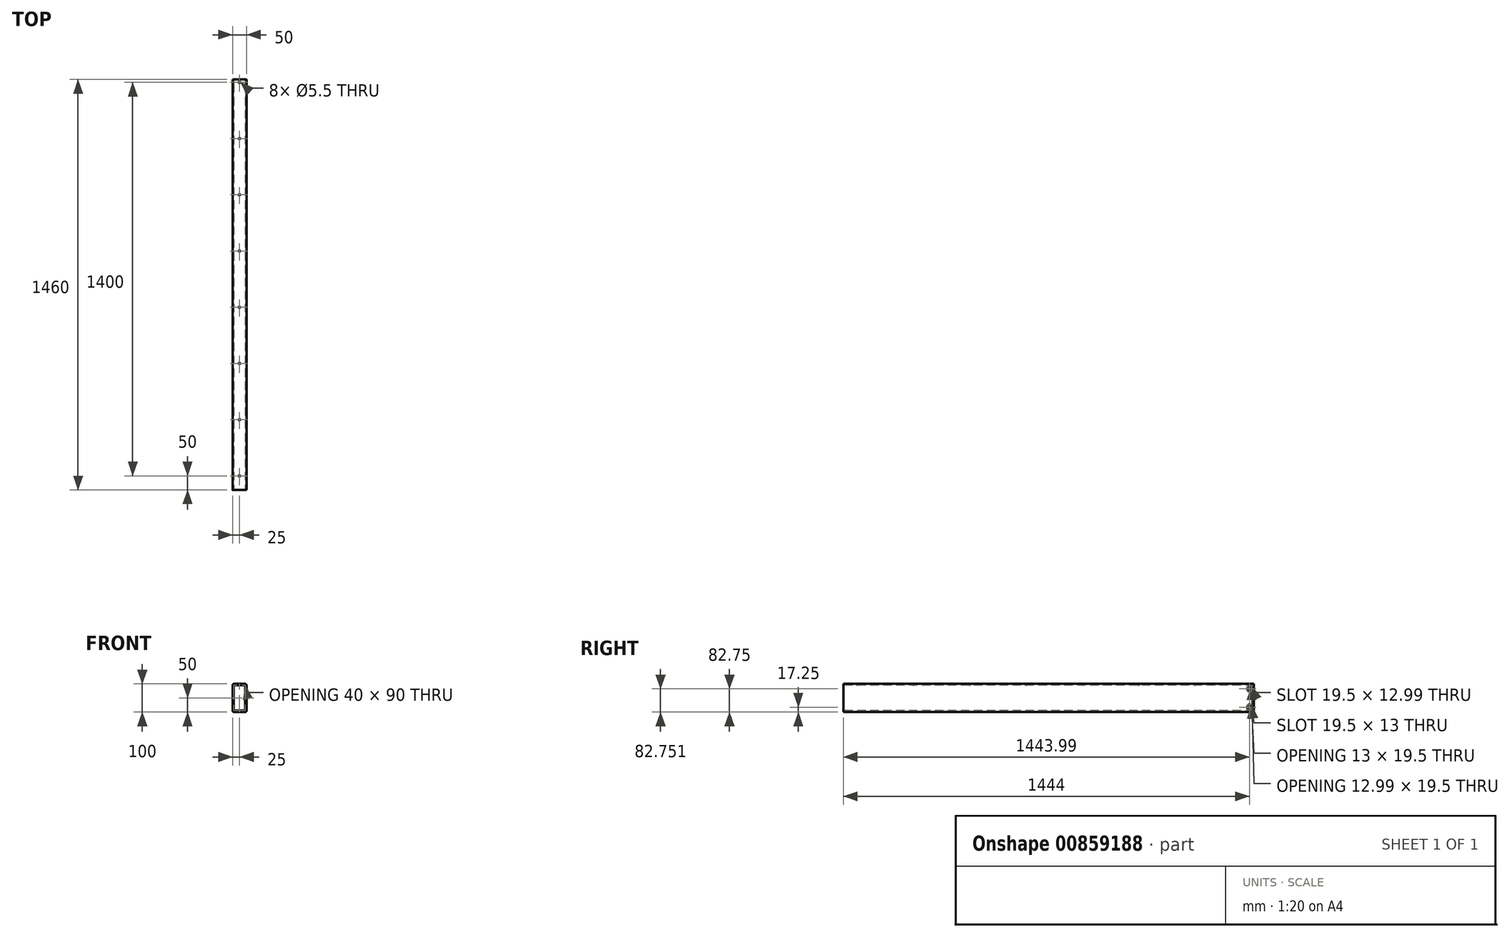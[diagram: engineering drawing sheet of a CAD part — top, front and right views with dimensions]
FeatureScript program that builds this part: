
annotation { "Feature Type Name" : "Feature", "Feature Type Description" : "" }
export const myFeature = defineFeature(function(context is Context, id is Id, definition is map)
    precondition{}
    {
        {
            var Q0;
            Q0=qCreatedBy(makeId("Front.planeOp"),FACE);
            var sketch = newSketch(context, id + "F0", { "sketchPlane" : qUnion([Q0])});
            skLineSegment(sketch, "E0.bottom", {"start": v(20, -50) * mm, "end": v(-20, -50) * mm});
            skLineSegment(sketch, "E0.top", {"start": v(20, 50) * mm, "end": v(-20, 50) * mm});
            skLineSegment(sketch, "E0.left", {"start": v(25, -45) * mm, "end": v(25, 45) * mm});
            skLineSegment(sketch, "E0.right", {"start": v(-25, -45) * mm, "end": v(-25, 45) * mm});
            skPoint(sketch, "E0.middle", {"position": v(0, 0) * mm});
            skPoint(sketch, "E1.visualSharp", {"position": v(-25, 50) * mm});
            skArc(sketch, "E1.filletArc", {"start": v(-20, 50) * mm, "mid": v(-23.54, 48.54) * mm, "end": v(-25, 45) * mm});
            skPoint(sketch, "E2.visualSharp", {"position": v(25, 50) * mm});
            skArc(sketch, "E2.filletArc", {"start": v(25, 45) * mm, "mid": v(23.54, 48.54) * mm, "end": v(20, 50) * mm});
            skPoint(sketch, "E3.visualSharp", {"position": v(-25, -50) * mm});
            skArc(sketch, "E3.filletArc", {"start": v(-25, -45) * mm, "mid": v(-23.54, -48.54) * mm, "end": v(-20, -50) * mm});
            skPoint(sketch, "E4.visualSharp", {"position": v(25, -50) * mm});
            skArc(sketch, "E4.filletArc", {"start": v(20, -50) * mm, "mid": v(23.54, -48.54) * mm, "end": v(25, -45) * mm});
            skLineSegment(sketch, "E5.0", {"start": v(-20, -42.5) * mm, "end": v(-20, 42.5) * mm});
            skLineSegment(sketch, "E5.1", {"start": v(17.5, -45) * mm, "end": v(-17.5, -45) * mm});
            skLineSegment(sketch, "E5.2", {"start": v(20, -42.5) * mm, "end": v(20, 42.5) * mm});
            skLineSegment(sketch, "E5.3", {"start": v(17.5, 45) * mm, "end": v(-17.5, 45) * mm});
            skArc(sketch, "E6.filletArc", {"start": v(-17.5, 45) * mm, "mid": v(-19.27, 44.27) * mm, "end": v(-20, 42.5) * mm});
            skArc(sketch, "E7.filletArc", {"start": v(20, 42.5) * mm, "mid": v(19.27, 44.27) * mm, "end": v(17.5, 45) * mm});
            skArc(sketch, "E8.filletArc", {"start": v(17.5, -45) * mm, "mid": v(19.27, -44.27) * mm, "end": v(20, -42.5) * mm});
            skArc(sketch, "E9.filletArc", {"start": v(-20, -42.5) * mm, "mid": v(-19.27, -44.27) * mm, "end": v(-17.5, -45) * mm});
            skSolve(sketch);
        }
        {
            var Q0;
            Q0=makeQuery(id+"F0.imprint","IMPRINT",FACE,{"disambiguationData":[TD([[makeQuery(id+"F0.imprint","IMPRINT",EDGE,{"derivedFrom":sQuery(id+"F0.wireOp",EDGE,"E0.bottom")}),-1.0]])]});
            extrude(context, id + "F1", {"entities" : qUnion([Q0]), "oppositeDirection" : true, "depth" : 1460 * mm, "offsetDistance" : 25 * mm});
        }
        {
            var Q0;
            Q0=makeQuery(id+"F1.opExtrude","SWEPT_FACE",FACE,{"disambiguationData":[OSD([sQuery(id+"F0.wireOp",EDGE,"E0.top")])]});
            var sketch = newSketch(context, id + "F2", { "sketchPlane" : qUnion([Q0])});
            skCircle(sketch, "E10", {"center": v(0, 50) * mm, "radius": 1.12 * mm});
            skCircle(sketch, "E11.0.1.0", {"center": v(0, 250) * mm, "radius": 1.12 * mm});
            skCircle(sketch, "E11.0.2.0", {"center": v(0, 450) * mm, "radius": 1.12 * mm});
            skCircle(sketch, "E11.0.3.0", {"center": v(0, 650) * mm, "radius": 1.12 * mm});
            skCircle(sketch, "E11.0.4.0", {"center": v(0, 850) * mm, "radius": 1.12 * mm});
            skCircle(sketch, "E11.0.5.0", {"center": v(0, 1050) * mm, "radius": 1.12 * mm});
            skCircle(sketch, "E11.0.6.0", {"center": v(0, 1250) * mm, "radius": 1.12 * mm});
            skCircle(sketch, "E11.0.7.0", {"center": v(0, 1450) * mm, "radius": 1.12 * mm});
            skLineSegment(sketch, "E11.direction1", {"start": v(0, 50) * mm, "end": v(25, 50) * mm, "construction": true});
            skLineSegment(sketch, "E11.direction2", {"start": v(0, 50) * mm, "end": v(0, 250) * mm, "construction": true});
            skSolve(sketch);
        }
        {
            var Q0;
            Q0=sQuery(id+"F2.wireOp",VERTEX,"E11.direction1.start");
            var Q1;
            Q1=sQuery(id+"F2.wireOp",VERTEX,"E11.direction2.end");
            var Q2;
            Q2=sQuery(id+"F2.wireOp",VERTEX,"E11.0.2.0.center");
            var Q3;
            Q3=sQuery(id+"F2.wireOp",VERTEX,"E11.0.3.0.center");
            var Q4;
            Q4=sQuery(id+"F2.wireOp",VERTEX,"E11.0.4.0.center");
            var Q5;
            Q5=sQuery(id+"F2.wireOp",VERTEX,"E11.0.5.0.center");
            var Q6;
            Q6=sQuery(id+"F2.wireOp",VERTEX,"E11.0.6.0.center");
            var Q7;
            Q7=sQuery(id+"F2.wireOp",VERTEX,"E11.0.7.0.center");
            var Q8;
            Q8=sQuery(id+"F2.wireOp",VERTEX,"E11.0.8.0.center");
            var Q9;
            Q9=sQuery(id+"F2.wireOp",VERTEX,"E11.0.9.0.center");
            var Q10;
            Q10=makeQuery(id+"F1.opExtrude","SWEPT_BODY",BODY,{"disambiguationData":[OSD([sQuery(id+"F0.wireOp",EDGE,"E0.bottom"),sQuery(id+"F0.wireOp",EDGE,"E0.top"),sQuery(id+"F0.wireOp",EDGE,"E0.left"),sQuery(id+"F0.wireOp",EDGE,"E0.right"),sQuery(id+"F0.wireOp",EDGE,"E1.filletArc"),sQuery(id+"F0.wireOp",EDGE,"E2.filletArc"),sQuery(id+"F0.wireOp",EDGE,"E3.filletArc"),sQuery(id+"F0.wireOp",EDGE,"E4.filletArc"),sQuery(id+"F0.wireOp",EDGE,"E5.0"),sQuery(id+"F0.wireOp",EDGE,"E5.1"),sQuery(id+"F0.wireOp",EDGE,"E5.2"),sQuery(id+"F0.wireOp",EDGE,"E5.3"),sQuery(id+"F0.wireOp",EDGE,"E6.filletArc"),sQuery(id+"F0.wireOp",EDGE,"E7.filletArc"),sQuery(id+"F0.wireOp",EDGE,"E8.filletArc"),sQuery(id+"F0.wireOp",EDGE,"E9.filletArc")])]});
            hole(context, id + "F3", {"style" : HoleStyle.SIMPLE, "endStyle" : HoleEndStyle.BLIND, "standardTappedOrClearance" : lookupTablePath({ "fit" : "Normal", "standard" : "ISO", "size" : "M5", "type" : "Clearance" }), "standardBlindInLast" : lookupTablePath({ "fit" : "Standard", "standard" : "ISO", "size" : "M5", "type" : "Clearance" }), "holeDiameter" : 5.5 * mm, "majorDiameter" : 5 * mm, "holeDepth" : 14.4 * mm, "isTappedThrough" : true, "tappedDepth" : 12 * mm, "tapClearance" : 3, "locations" : qUnion([Q0, Q1, Q2, Q3, Q4, Q5, Q6, Q7, Q8, Q9]), "scope" : qUnion([Q10])});
        }
        {
            var Q0;
            Q0=makeQuery(id+"F1.opExtrude","SWEPT_FACE",FACE,{"disambiguationData":[OSD([sQuery(id+"F0.wireOp",EDGE,"E0.left")])]});
            var sketch = newSketch(context, id + "F4", { "sketchPlane" : qUnion([Q0])});
            skArc(sketch, "E12", {"start": v(1450.49, 35.63) * mm, "mid": v(1444.15, 42.5) * mm, "end": v(1437.5, 35.93) * mm});
            skArc(sketch, "E13", {"start": v(1437.5, -36) * mm, "mid": v(1444, -42.5) * mm, "end": v(1450.5, -36) * mm});
            skArc(sketch, "E14", {"start": v(1437.5, 29.57) * mm, "mid": v(1444.15, 23) * mm, "end": v(1450.49, 29.87) * mm});
            skArc(sketch, "E15", {"start": v(1450.5, -29.63) * mm, "mid": v(1444.01, -23) * mm, "end": v(1437.5, -29.6) * mm});
            skLineSegment(sketch, "E16", {"start": v(1437.5, 35.93) * mm, "end": v(1437.5, 29.57) * mm});
            skLineSegment(sketch, "E17", {"start": v(1450.49, 35.63) * mm, "end": v(1450.49, 29.87) * mm});
            skLineSegment(sketch, "E18", {"start": v(1437.5, -29.6) * mm, "end": v(1437.5, -36) * mm});
            skLineSegment(sketch, "E19", {"start": v(1450.5, -29.63) * mm, "end": v(1450.5, -36) * mm});
            skSolve(sketch);
        }
        {
            var Q0;
            {var subQ3=sQuery(id+"F4.wireOp",EDGE,"E14");Q0=makeQuery(id+"F4.imprint","IMPRINT",FACE,{"disambiguationData":[TD([[makeQuery(id+"F4.imprint","IMPRINT",EDGE,{"derivedFrom":subQ3}),1.0]])]});}
            var Q1;
            {var subQ4=sQuery(id+"F4.wireOp",EDGE,"E13");Q1=makeQuery(id+"F4.imprint","IMPRINT",FACE,{"disambiguationData":[TD([[makeQuery(id+"F4.imprint","IMPRINT",EDGE,{"derivedFrom":subQ4}),1.0]])]});}
            extrude(context, id + "F5", {"entities" : qUnion([Q0, Q1]), "operationType" : NewBodyOperationType.REMOVE, "endBound" : BoundingType.THROUGH_ALL, "oppositeDirection" : true, "depth" : 25 * mm, "offsetDistance" : 25 * mm});
        }
    });
